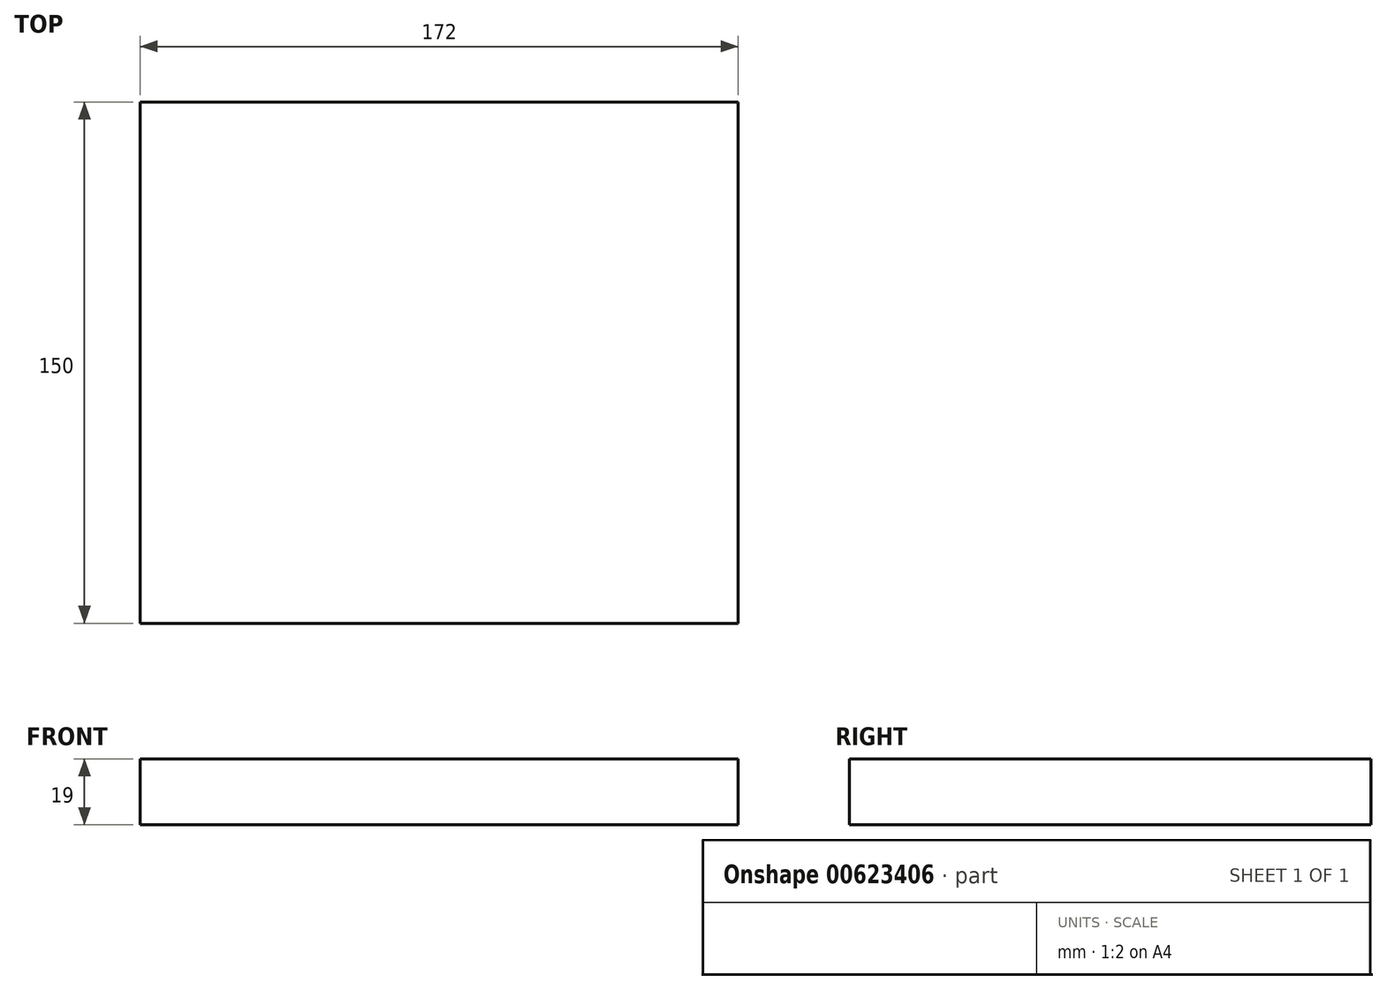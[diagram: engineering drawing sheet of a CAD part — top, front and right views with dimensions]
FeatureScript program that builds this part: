
annotation { "Feature Type Name" : "Feature", "Feature Type Description" : "" }
export const myFeature = defineFeature(function(context is Context, id is Id, definition is map)
    precondition{}
    {
        {
            var Q0;
            Q0=qCreatedBy(makeId("Top.planeOp"),FACE);
            var sketch = newSketch(context, id + "F0", { "sketchPlane" : qUnion([Q0])});
            skLineSegment(sketch, "E0.bottom", {"start": v(86, 75) * mm, "end": v(-86, 75) * mm});
            skLineSegment(sketch, "E0.top", {"start": v(86, -75) * mm, "end": v(-86, -75) * mm});
            skLineSegment(sketch, "E0.left", {"start": v(86, 75) * mm, "end": v(86, -75) * mm});
            skLineSegment(sketch, "E0.right", {"start": v(-86, 75) * mm, "end": v(-86, -75) * mm});
            skPoint(sketch, "E0.middle", {"position": v(0, 0) * mm});
            skSolve(sketch);
        }
        {
            var Q0;
            Q0=qSketchRegion(id+"F0",true);
            extrude(context, id + "F1", {"entities" : qUnion([Q0]), "depth" : 19 * mm, "offsetDistance" : 25 * mm});
        }
    });
